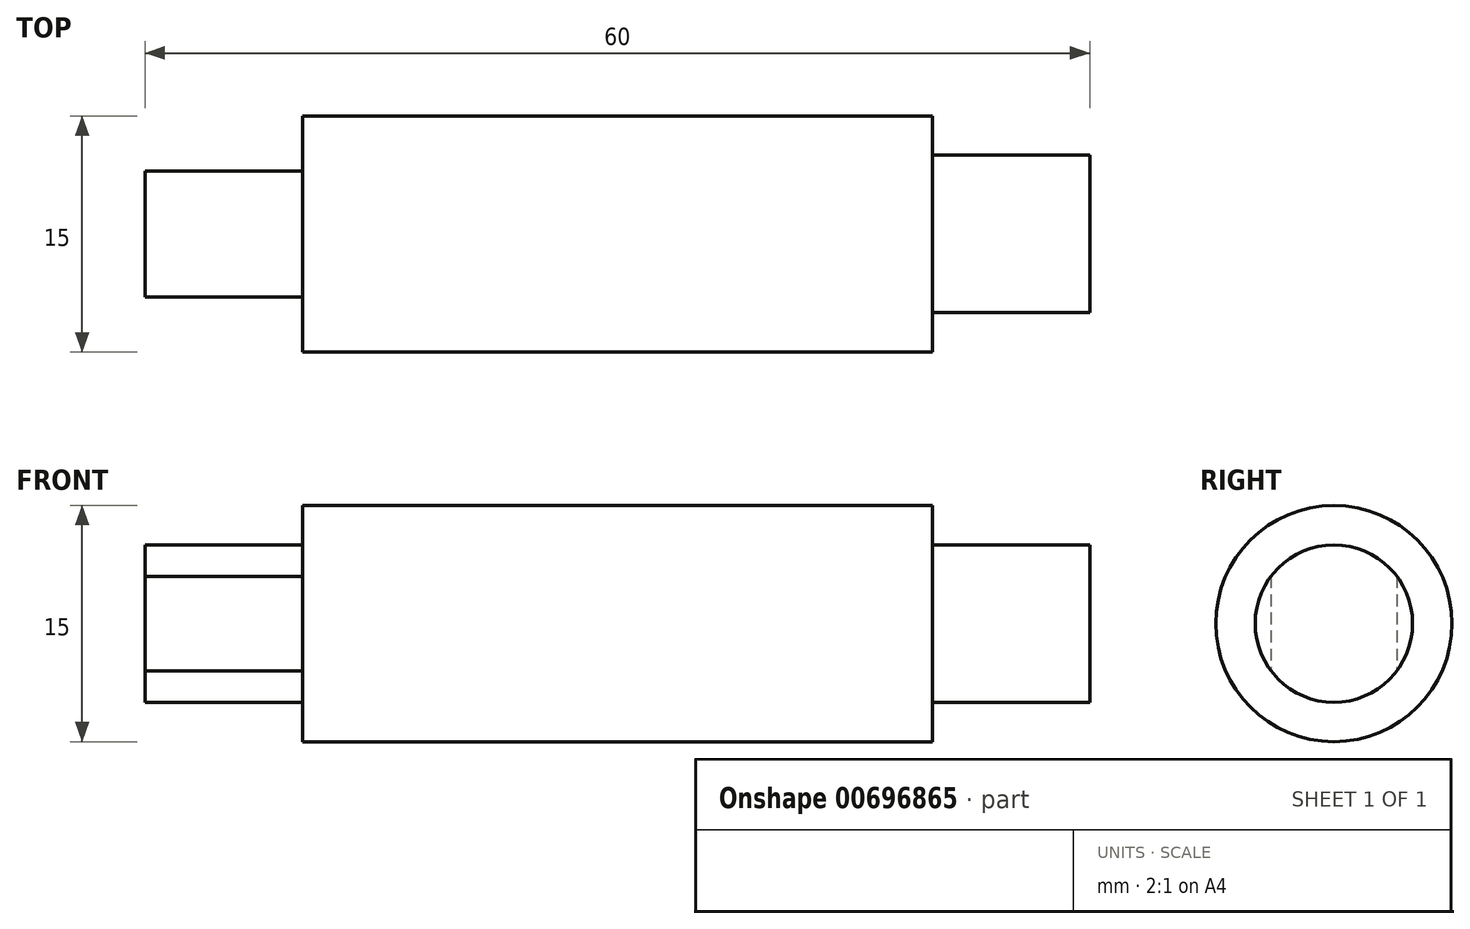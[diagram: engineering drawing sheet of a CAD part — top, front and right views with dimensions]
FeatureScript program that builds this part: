
annotation { "Feature Type Name" : "Feature", "Feature Type Description" : "" }
export const myFeature = defineFeature(function(context is Context, id is Id, definition is map)
    precondition{}
    {
        {
            var Q0;
            Q0=qCreatedBy(makeId("Right.planeOp"),FACE);
            var sketch = newSketch(context, id + "F0", { "sketchPlane" : qUnion([Q0])});
            skCircle(sketch, "E0", {"center": v(0, 0) * mm, "radius": 5 * mm});
            skSolve(sketch);
        }
        {
            var Q0;
            Q0 = qSketchRegion(id + "F0", true);
            extrude(context, id + "F1", {"entities" : qUnion([Q0]), "depth" : 50 * mm, "offsetDistance" : 25 * mm, "hasSecondDirection" : true, "secondDirectionOppositeDirection" : true, "secondDirectionDepth" : 10 * mm});
        }
        {
            var Q0;
            Q0=qCreatedBy(makeId("Right.planeOp"),FACE);
            var sketch = newSketch(context, id + "F2", { "sketchPlane" : qUnion([Q0])});
            skCircle(sketch, "E1", {"center": v(0, 0) * mm, "radius": 7.5 * mm});
            skSolve(sketch);
        }
        {
            var Q0;
            Q0 = qSketchRegion(id + "F2", true);
            extrude(context, id + "F3", {"entities" : qUnion([Q0]), "operationType" : NewBodyOperationType.ADD, "depth" : (50 - 10) * mm, "offsetDistance" : 25 * mm});
        }
        {
            var Q0;
            Q0=makeQuery(id+"F1.opExtrude","CAP_FACE",FACE,{"disambiguationData":[OSD([sQuery(id+"F0.wireOp",EDGE,"E0")])],"isStart":true});
            var sketch = newSketch(context, id + "F4", { "sketchPlane" : qUnion([Q0])});
            skArc(sketch, "E2.0", {"start": v(-4, 3) * mm, "mid": v(-5, 0) * mm, "end": v(-4, -3) * mm});
            skLineSegment(sketch, "E3", {"start": v(-4, 3) * mm, "end": v(-4, -3) * mm});
            skLineSegment(sketch, "E4", {"start": v(4, 3) * mm, "end": v(4, -3) * mm});
            skArc(sketch, "E5.trimOffspring", {"start": v(4, -3) * mm, "mid": v(5, 0) * mm, "end": v(4, 3) * mm});
            skSolve(sketch);
        }
        {
            var Q0;
            Q0 = qSketchRegion(id + "F4", true);
            var Q1;
            Q1=makeQuery(id+"F3.opExtrude","CAP_FACE",FACE,{"disambiguationData":[OSD([sQuery(id+"F2.wireOp",EDGE,"E1")])],"isStart":true});
            extrude(context, id + "F5", {"entities" : qUnion([Q0]), "operationType" : NewBodyOperationType.REMOVE, "endBound" : BoundingType.UP_TO_SURFACE, "oppositeDirection" : true, "depth" : 25 * mm, "endBoundEntityFace" : qUnion([Q1]), "offsetDistance" : 25 * mm});
        }
    });
